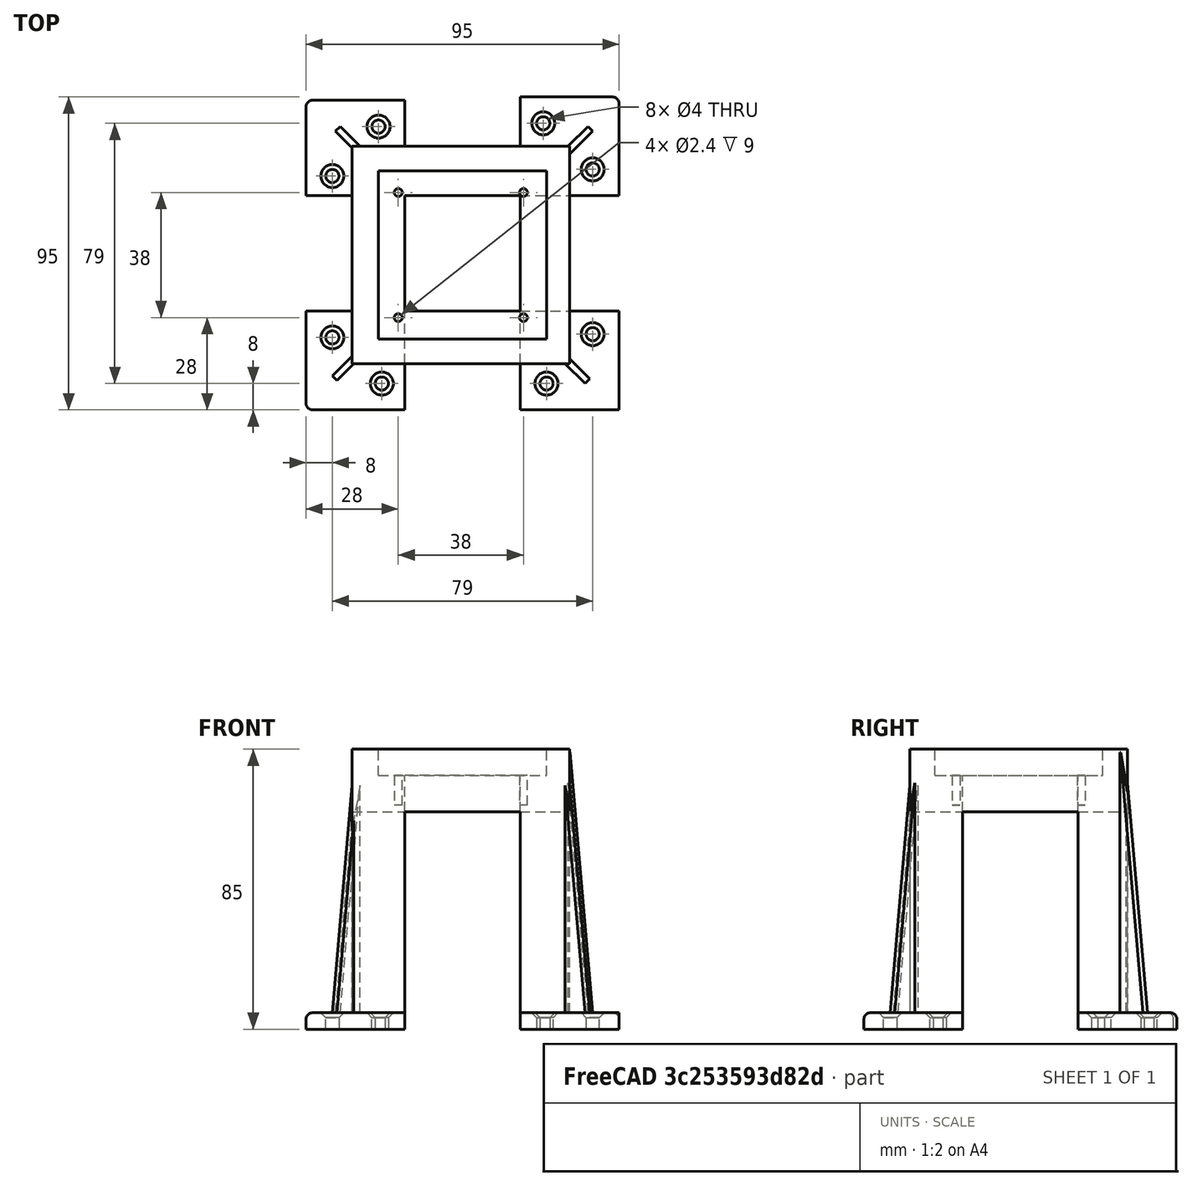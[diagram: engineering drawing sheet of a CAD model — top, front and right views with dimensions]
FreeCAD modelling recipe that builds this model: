
FCSTD DOCUMENT  (FreeCAD 0.20R29603 (Git))
Label: Torre_Cohete
License: All rights reserved
LicenseURL: http://en.wikipedia.org/wiki/All_rights_reserved
objects: Part::Cut×25, Part::Box×22, Part::Cylinder×14, Part::MultiFuse×10, Part::Chamfer×10, Part::Fillet×9
note: 90 computed .brp shape members not serialized (recipe doc carries the construction recipe); baked Part::Feature solids carry a one-line shape summary decoded from their .brp

FEATURE [Part::Box] Box012  label="Cubo012"
  AttacherType = Attacher::AttachEngine3D
  Height = 80
  Length = 2
  Placement = pos=(39,-39,-73) rot=(0,0,1;0rad)
  Width = 10
FEATURE [Part::Box] Box013  label="Cubo013"
  AttacherType = Attacher::AttachEngine3D
  Height = 150
  Length = 5
  Placement = pos=(39,-52.5,-100) rot=(-1,0,0;0.122173rad)
  Width = 10
FEATURE [Part::Box] Box014  label="Cubo014"
  AttacherType = Attacher::AttachEngine3D
  Height = 5
  Length = 30
  Placement = pos=(18,-47,-77) rot=(0,0,1;0rad)
  Width = 30
FEATURE [Part::Box] Box015  label="Cubo015"
  AttacherType = Attacher::AttachEngine3D
  Height = 80
  Length = 2
  Placement = pos=(39,-39,-73) rot=(0,0,1;0rad)
  Width = 10
FEATURE [Part::Box] Box016  label="Cubo016"
  AttacherType = Attacher::AttachEngine3D
  Height = 150
  Length = 5
  Placement = pos=(39,-52.5,-100) rot=(-1,0,0;0.122173rad)
  Width = 10
FEATURE [Part::Box] Box017  label="Cubo017"
  AttacherType = Attacher::AttachEngine3D
  Height = 5
  Length = 30
  Placement = pos=(18,-47,-77) rot=(0,0,1;0rad)
  Width = 30
FEATURE [Part::Box] Box018  label="Cubo018"
  AttacherType = Attacher::AttachEngine3D
  Height = 80
  Length = 2
  Placement = pos=(39,-39,-73) rot=(0,0,1;0rad)
  Width = 10
FEATURE [Part::Box] Box019  label="Cubo019"
  AttacherType = Attacher::AttachEngine3D
  Height = 150
  Length = 5
  Placement = pos=(39,-52.5,-100) rot=(-1,0,0;0.122173rad)
  Width = 10
FEATURE [Part::Box] Box020  label="Cubo020"
  AttacherType = Attacher::AttachEngine3D
  Height = 5
  Length = 30
  Placement = pos=(18,-47,-77) rot=(0,0,1;0rad)
  Width = 30
FEATURE [Part::Box] Box021  label="Cubo021"
  AttacherType = Attacher::AttachEngine3D
  Height = 80
  Length = 2
  Placement = pos=(39,-39,-73) rot=(0,0,1;0rad)
  Width = 10
FEATURE [Part::Box] Box022  label="Cubo022"
  AttacherType = Attacher::AttachEngine3D
  Height = 150
  Length = 5
  Placement = pos=(39,-52.5,-100) rot=(-1,0,0;0.122173rad)
  Width = 10
FEATURE [Part::Box] Box023  label="Cubo023"
  AttacherType = Attacher::AttachEngine3D
  Height = 10
  Length = 60
  Placement = pos=(-49,-42,-80) rot=(0,0,1;0rad)
  Width = 60
FEATURE [Part::Box] Box237  label="Cubo223"
  AttacherType = Attacher::AttachEngine3D
  Height = 85
  Length = 66
  Placement = pos=(-33,-33,-77) rot=(0,0,1;0rad)
  Width = 66
FEATURE [Part::Box] Box238  label="Cubo224"
  AttacherType = Attacher::AttachEngine3D
  Height = 8
  Length = 50
  Placement = pos=(-25,-25,0) rot=(0,0,1;0rad)
  Width = 50
FEATURE [Part::Box] Box239  label="Cubo225"
  AttacherType = Attacher::AttachEngine3D
  Height = 89
  Length = 35
  Placement = pos=(-17,-17,-81) rot=(0,0,1;0rad)
  Width = 35
FEATURE [Part::Box] Box240  label="Cubo226"
  AttacherType = Attacher::AttachEngine3D
  Height = 89
  Length = 80
  Placement = pos=(-39,-17,-100) rot=(0,0,1;0rad)
  Width = 35
FEATURE [Part::Box] Box241  label="Cubo227"
  AttacherType = Attacher::AttachEngine3D
  Height = 89
  Length = 35
  Placement = pos=(-17,-40,-100) rot=(0,0,1;0rad)
  Width = 100
FEATURE [Part::Box] Box242  label="Cubo228"
  AttacherType = Attacher::AttachEngine3D
  Height = 10
  Length = 51
  Placement = pos=(-25,-25.5,0) rot=(0,0,1;0rad)
  Width = 51
FEATURE [Part::Box] Box243  label="Cubo229"
  AttacherType = Attacher::AttachEngine3D
  Height = 5
  Length = 30
  Placement = pos=(18,-47,-77) rot=(0,0,1;0rad)
  Width = 30
FEATURE [Part::Box] Box244  label="Cubo230"
  AttacherType = Attacher::AttachEngine3D
  Height = 80
  Length = 2
  Placement = pos=(39,-39,-73) rot=(0,0,1;0rad)
  Width = 10
FEATURE [Part::Box] Box245  label="Cubo231"
  AttacherType = Attacher::AttachEngine3D
  Height = 150
  Length = 5
  Placement = pos=(39,-52.5,-100) rot=(-1,0,0;0.122173rad)
  Width = 10
FEATURE [Part::Box] Box246  label="Cubo232"
  AttacherType = Attacher::AttachEngine3D
  Height = 5
  Length = 30
  Placement = pos=(18,-47,-77) rot=(0,0,1;0rad)
  Width = 30
FEATURE [Part::Cut] Cut007
  Base = -> Box237
  Tool = -> Box238
FEATURE [Part::Cut] Cut008
  Base = -> Cut007
  Tool = -> Box239
FEATURE [Part::Cut] Cut009
  Base = -> Cut008
  Tool = -> Box240
FEATURE [Part::Cut] Cut010
  Base = -> Cut009
  Tool = -> Box241
FEATURE [Part::Cut] Cut011
  Base = -> Cut010
  Tool = -> Box242
FEATURE [Part::Cut] Cut015
  Base = -> Box012
  Placement = pos=(-17.5,-39,0) rot=(0,0,1;0.785398rad)
  Tool = -> Box013
FEATURE [Part::Cut] Cut018
  Base = -> Box015
  Placement = pos=(-17.5,-39,0) rot=(0,0,1;0.785398rad)
  Tool = -> Box016
FEATURE [Part::Cut] Cut021
  Base = -> Box018
  Placement = pos=(-17.5,-39,0) rot=(0,0,1;0.785398rad)
  Tool = -> Box019
FEATURE [Part::Cut] Cut024
  Base = -> Box021
  Placement = pos=(-17.5,-39,0) rot=(0,0,1;0.785398rad)
  Tool = -> Box022
FEATURE [Part::Cut] Cut275
  Base = -> Box244
  Placement = pos=(-17.5,-39,0) rot=(0,0,1;0.785398rad)
  Tool = -> Box245
FEATURE [Part::Cylinder] Cylinder012  label="Cilindro012"
  Angle = 360
  AttacherType = Attacher::AttachEngine3D
  FirstAngle = 0
  Height = 10
  Placement = pos=(40,-24,-80) rot=(0,0,1;0rad)
  Radius = 2
  SecondAngle = 0
FEATURE [Part::Cylinder] Cylinder013  label="Cilindro013"
  Angle = 360
  AttacherType = Attacher::AttachEngine3D
  FirstAngle = 0
  Height = 10
  Placement = pos=(26,-39,-80) rot=(0,0,1;0rad)
  Radius = 2
  SecondAngle = 0
FEATURE [Part::Cylinder] Cylinder014  label="Cilindro014"
  Angle = 360
  AttacherType = Attacher::AttachEngine3D
  FirstAngle = 0
  Height = 10
  Placement = pos=(40,-24,-80) rot=(0,0,1;0rad)
  Radius = 2
  SecondAngle = 0
FEATURE [Part::Cylinder] Cylinder015  label="Cilindro015"
  Angle = 360
  AttacherType = Attacher::AttachEngine3D
  FirstAngle = 0
  Height = 10
  Placement = pos=(26,-39,-80) rot=(0,0,1;0rad)
  Radius = 2
  SecondAngle = 0
FEATURE [Part::Cylinder] Cylinder016  label="Cilindro016"
  Angle = 360
  AttacherType = Attacher::AttachEngine3D
  FirstAngle = 0
  Height = 10
  Placement = pos=(40,-24,-80) rot=(0,0,1;0rad)
  Radius = 2
  SecondAngle = 0
FEATURE [Part::Cylinder] Cylinder017  label="Cilindro017"
  Angle = 360
  AttacherType = Attacher::AttachEngine3D
  FirstAngle = 0
  Height = 10
  Placement = pos=(26,-39,-80) rot=(0,0,1;0rad)
  Radius = 2
  SecondAngle = 0
FEATURE [Part::Cylinder] Cylinder018  label="Cilindro018"
  Angle = 360
  AttacherType = Attacher::AttachEngine3D
  FirstAngle = 0
  Height = 10
  Placement = pos=(-19,-19,-9) rot=(0,0,1;0rad)
  Radius = 1.2
  SecondAngle = 0
FEATURE [Part::Cylinder] Cylinder019  label="Cilindro019"
  Angle = 360
  AttacherType = Attacher::AttachEngine3D
  FirstAngle = 0
  Height = 10
  Placement = pos=(19,-19,-9) rot=(0,0,1;0rad)
  Radius = 1.2
  SecondAngle = 0
FEATURE [Part::Cylinder] Cylinder020  label="Cilindro020"
  Angle = 360
  AttacherType = Attacher::AttachEngine3D
  FirstAngle = 0
  Height = 10
  Placement = pos=(19,19,-9) rot=(0,0,1;0rad)
  Radius = 1.2
  SecondAngle = 0
FEATURE [Part::Cylinder] Cylinder021  label="Cilindro021"
  Angle = 360
  AttacherType = Attacher::AttachEngine3D
  FirstAngle = 0
  Height = 10
  Placement = pos=(-19,19,-9) rot=(0,0,1;0rad)
  Radius = 1.2
  SecondAngle = 0
FEATURE [Part::Cylinder] Cylinder198  label="Cilindro198"
  Angle = 360
  AttacherType = Attacher::AttachEngine3D
  FirstAngle = 0
  Height = 10
  Placement = pos=(40,-24,-80) rot=(0,0,1;0rad)
  Radius = 2
  SecondAngle = 0
FEATURE [Part::Cylinder] Cylinder199  label="Cilindro199"
  Angle = 360
  AttacherType = Attacher::AttachEngine3D
  FirstAngle = 0
  Height = 10
  Placement = pos=(26,-39,-80) rot=(0,0,1;0rad)
  Radius = 2
  SecondAngle = 0
FEATURE [Part::Cylinder] Cylinder200  label="Cilindro200"
  Angle = 360
  AttacherType = Attacher::AttachEngine3D
  FirstAngle = 0
  Height = 10
  Placement = pos=(40,-24,-80) rot=(0,0,1;0rad)
  Radius = 2
  SecondAngle = 0
FEATURE [Part::Cylinder] Cylinder201  label="Cilindro201"
  Angle = 360
  AttacherType = Attacher::AttachEngine3D
  FirstAngle = 0
  Height = 10
  Placement = pos=(26,-39,-80) rot=(0,0,1;0rad)
  Radius = 2
  SecondAngle = 0
FEATURE [Part::MultiFuse] Fusion147
  Shapes = -> [Box243,Cut275]
FEATURE [Part::Cut] Cut276
  Base = -> Fusion147
  Tool = -> Cylinder198
FEATURE [Part::Cut] Cut014
  Base = -> Cut276
  Tool = -> Cylinder199
FEATURE [Part::Chamfer] Chamfer009
  Base = -> Cut014
  Edges = 1 edges r=1.5: [Edge10]
FEATURE [Part::Chamfer] Chamfer010
  Base = -> Chamfer009
  Edges = 1 edges r=1.5: [Edge10]
FEATURE [Part::Fillet] Fillet175
  Base = -> Chamfer010
  Edges = 1 edges r=2: [Edge4]
FEATURE [Part::Fillet] Fillet176
  Base = -> Fillet175
  Edges = 1 edges r=2: [Edge3]
FEATURE [Part::MultiFuse] Fusion148
  Shapes = -> [Box246,Cut015]
FEATURE [Part::Cut] Cut277
  Base = -> Fusion148
  Tool = -> Cylinder200
FEATURE [Part::Cut] Cut278
  Base = -> Cut277
  Tool = -> Cylinder201
FEATURE [Part::Chamfer] Chamfer011
  Base = -> Cut278
  Edges = 1 edges r=1.5: [Edge10]
FEATURE [Part::Chamfer] Chamfer012
  Base = -> Chamfer011
  Edges = 1 edges r=1.5: [Edge10]
FEATURE [Part::Fillet] Fillet177
  Base = -> Chamfer012
  Edges = 1 edges r=2: [Edge4]
FEATURE [Part::Fillet] Fillet008
  Base = -> Fillet177
  Edges = 1 edges r=2: [Edge3]
  Placement = pos=(1,0,0) rot=(0,0,1;1.5708rad)
FEATURE [Part::MultiFuse] Fusion149
  Shapes = -> [Box014,Cut018]
FEATURE [Part::Cut] Cut019
  Base = -> Fusion149
  Tool = -> Cylinder012
FEATURE [Part::Cut] Cut020
  Base = -> Cut019
  Tool = -> Cylinder013
FEATURE [Part::Chamfer] Chamfer013
  Base = -> Cut020
  Edges = 1 edges r=1.5: [Edge10]
FEATURE [Part::Chamfer] Chamfer014
  Base = -> Chamfer013
  Edges = 1 edges r=1.5: [Edge10]
FEATURE [Part::Fillet] Fillet178
  Base = -> Chamfer014
  Edges = 1 edges r=2: [Edge4]
FEATURE [Part::MultiFuse] Fusion150
  Shapes = -> [Box017,Cut021]
FEATURE [Part::Cut] Cut022
  Base = -> Fusion150
  Tool = -> Cylinder014
FEATURE [Part::Cut] Cut023
  Base = -> Cut022
  Tool = -> Cylinder015
FEATURE [Part::Chamfer] Chamfer015
  Base = -> Cut023
  Edges = 1 edges r=1.5: [Edge10]
FEATURE [Part::Chamfer] Chamfer016
  Base = -> Chamfer015
  Edges = 1 edges r=1.5: [Edge10]
FEATURE [Part::Fillet] Fillet179
  Base = -> Chamfer016
  Edges = 1 edges r=2: [Edge4]
FEATURE [Part::Fillet] Fillet180
  Base = -> Fillet179
  Edges = 1 edges r=2: [Edge3]
  Placement = pos=(1,0,0) rot=(0,0,1;3.14159rad)
FEATURE [Part::Cut] Cut027
  Base = -> Fillet180
  Tool = -> Box023
FEATURE [Part::MultiFuse] Fusion151
  Shapes = -> [Box020,Cut024]
FEATURE [Part::Cut] Cut025
  Base = -> Fusion151
  Tool = -> Cylinder016
FEATURE [Part::Cut] Cut026
  Base = -> Cut025
  Tool = -> Cylinder017
FEATURE [Part::Chamfer] Chamfer017
  Base = -> Cut026
  Edges = 1 edges r=1.5: [Edge10]
FEATURE [Part::Chamfer] Chamfer018
  Base = -> Chamfer017
  Edges = 1 edges r=1.5: [Edge10]
FEATURE [Part::Fillet] Fillet181
  Base = -> Chamfer018
  Edges = 1 edges r=2: [Edge4]
FEATURE [Part::Fillet] Fillet182
  Base = -> Fillet181
  Edges = 1 edges r=2: [Edge3]
  Placement = pos=(0,1,0) rot=(0,0,-1;1.5708rad)
FEATURE [Part::MultiFuse] Fusion152
  Shapes = -> [Cut011,Fillet176]
FEATURE [Part::MultiFuse] Fusion153
  Shapes = -> [Fusion152,Cut027]
FEATURE [Part::MultiFuse] Fusion154
  Shapes = -> [Fusion153,Fillet182]
FEATURE [Part::MultiFuse] Fusion155
  Shapes = -> [Fusion154,Fillet178]
FEATURE [Part::MultiFuse] Fusion011  label="BasePricipal"
  Shapes = -> [Fusion155,Fillet008]
FEATURE [Part::Cut] Cut028
  Base = -> Fusion011
  Tool = -> Cylinder018
FEATURE [Part::Cut] Cut029
  Base = -> Cut028
  Tool = -> Cylinder021
FEATURE [Part::Cut] Cut030
  Base = -> Cut029
  Tool = -> Cylinder020
FEATURE [Part::Cut] Cut031  label="Torre_Cohete"
  Base = -> Cut030
  Placement = pos=(-2,0,42) rot=(0,0,1;0rad)
  Tool = -> Cylinder019
